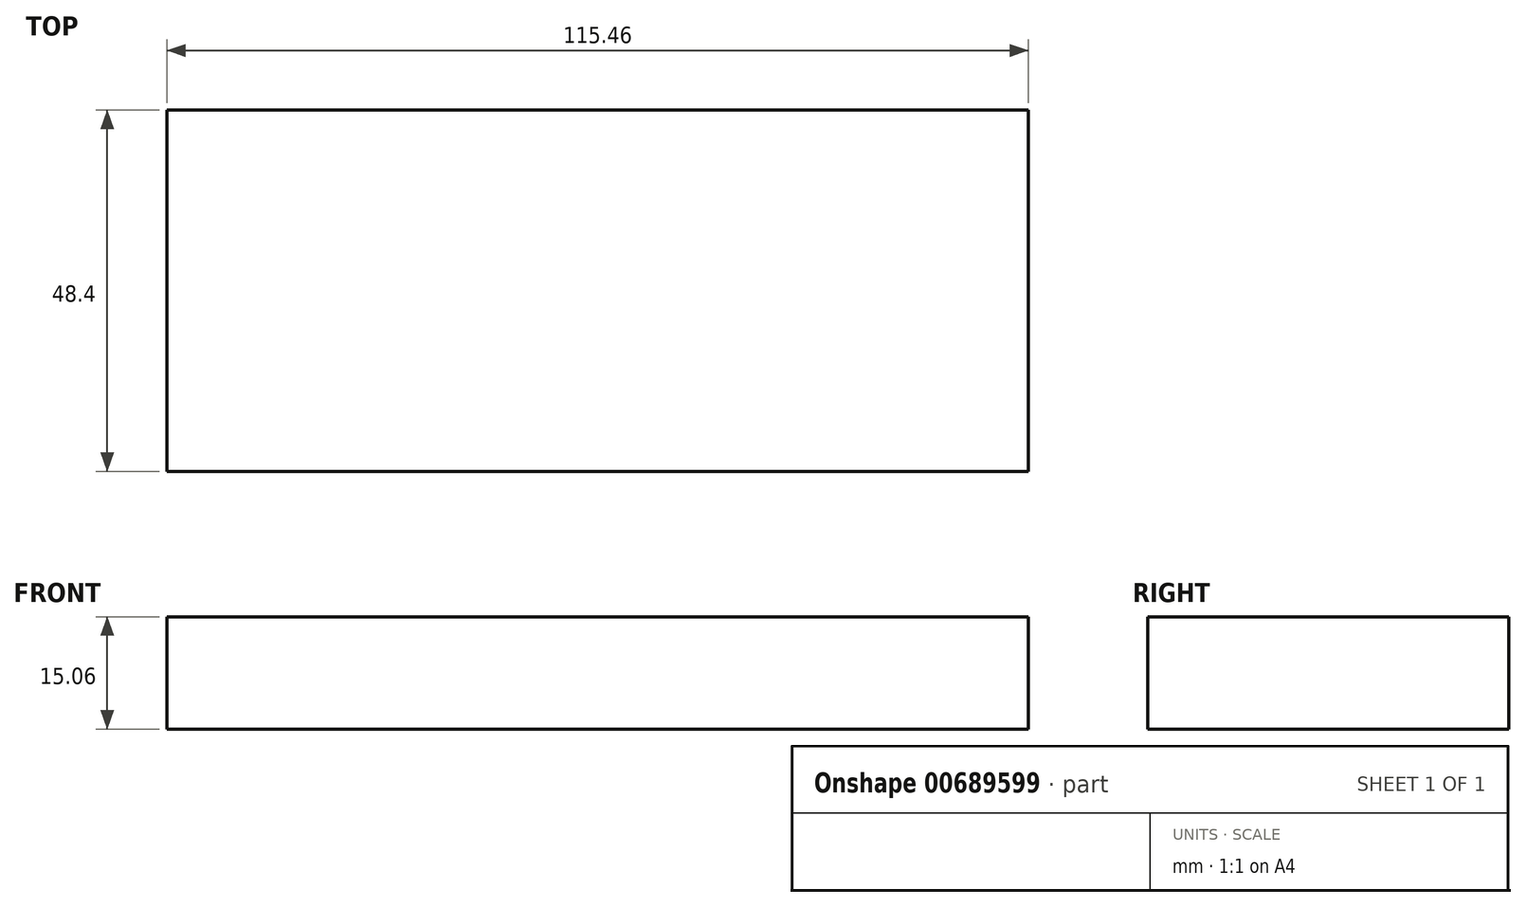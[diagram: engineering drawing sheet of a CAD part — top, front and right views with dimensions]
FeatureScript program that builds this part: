
annotation { "Feature Type Name" : "Feature", "Feature Type Description" : "" }
export const myFeature = defineFeature(function(context is Context, id is Id, definition is map)
    precondition{}
    {
        {
            var Q0;
            Q0=qCreatedBy(makeId("Front.planeOp"),FACE);
            var sketch = newSketch(context, id + "F0", { "sketchPlane" : qUnion([Q0])});
            skLineSegment(sketch, "E0.bottom", {"start": v(-39.92, 34.5) * mm, "end": v(75.54, 34.5) * mm});
            skLineSegment(sketch, "E0.top", {"start": v(-39.92, 19.44) * mm, "end": v(75.54, 19.44) * mm});
            skLineSegment(sketch, "E0.left", {"start": v(-39.92, 34.5) * mm, "end": v(-39.92, 19.44) * mm});
            skLineSegment(sketch, "E0.right", {"start": v(75.54, 34.5) * mm, "end": v(75.54, 19.44) * mm});
            skLineSegment(sketch, "E1.bottom", {"start": v(-122.45, -66.35) * mm, "end": v(-133.32, -66.35) * mm});
            skLineSegment(sketch, "E1.top", {"start": v(-122.45, -68.65) * mm, "end": v(-133.32, -68.65) * mm});
            skLineSegment(sketch, "E1.left", {"start": v(-122.45, -66.35) * mm, "end": v(-122.45, -68.65) * mm});
            skLineSegment(sketch, "E1.right", {"start": v(-133.32, -66.35) * mm, "end": v(-133.32, -68.65) * mm});
            skSolve(sketch);
        }
        {
            var Q0;
            Q0=makeQuery(id+"F0.imprint","IMPRINT",FACE,{"disambiguationData":[TD([[makeQuery(id+"F0.imprint","IMPRINT",EDGE,{"derivedFrom":sQuery(id+"F0.wireOp",EDGE,"E0.bottom")}),-1.0]])]});
            extrude(context, id + "F1", {"entities" : qUnion([Q0]), "oppositeDirection" : true, "depth" : 48.4 * mm, "offsetDistance" : 25.4 * mm});
        }
    });
